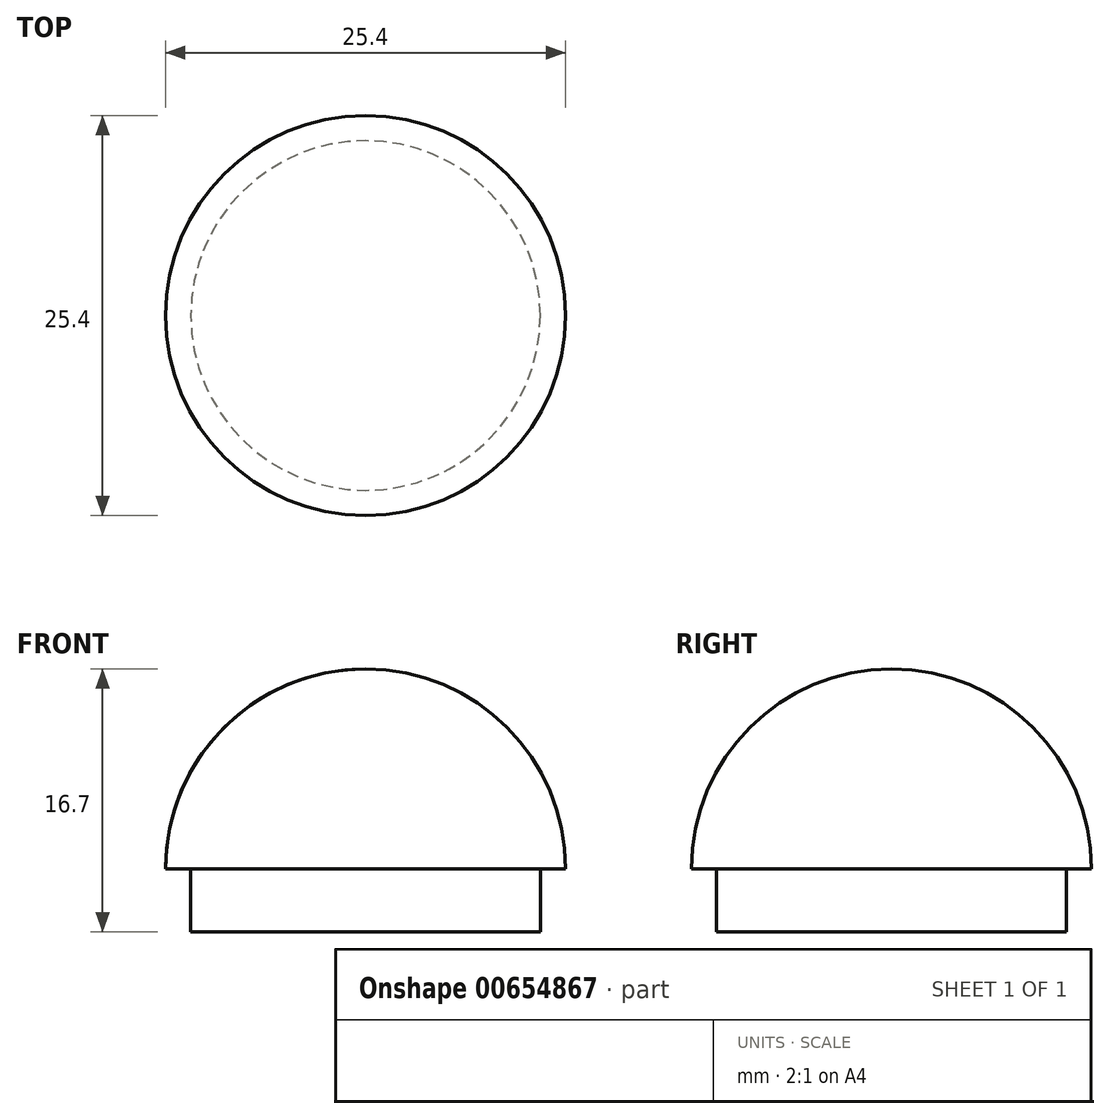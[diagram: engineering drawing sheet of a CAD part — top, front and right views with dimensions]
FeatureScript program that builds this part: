
annotation { "Feature Type Name" : "Feature", "Feature Type Description" : "" }
export const myFeature = defineFeature(function(context is Context, id is Id, definition is map)
    precondition{}
    {
        {
            var Q0;
            Q0=qCreatedBy(makeId("Front.planeOp"),FACE);
            var sketch = newSketch(context, id + "F0", { "sketchPlane" : qUnion([Q0])});
            skLineSegment(sketch, "E0", {"start": v(0, 0) * mm, "end": v(-11.1, 0) * mm});
            skLineSegment(sketch, "E1", {"start": v(-11.1, 0) * mm, "end": v(-11.1, 4) * mm});
            skLineSegment(sketch, "E2", {"start": v(-11.1, 4) * mm, "end": v(-12.7, 4) * mm});
            skLineSegment(sketch, "E3.MirrorCS", {"start": v(11.1, 4) * mm, "end": v(12.7, 4) * mm});
            skLineSegment(sketch, "E4.MirrorCS", {"start": v(11.1, 0) * mm, "end": v(11.1, 4) * mm});
            skLineSegment(sketch, "E5.MirrorCS", {"start": v(0, 0) * mm, "end": v(11.1, 0) * mm});
            skArc(sketch, "E6", {"start": v(12.7, 4) * mm, "mid": v(0, 16.7) * mm, "end": v(-12.7, 4) * mm});
            skLineSegment(sketch, "E7", {"start": v(0, 0) * mm, "end": v(0, 16.7) * mm});
            skSolve(sketch);
        }
        {
            var Q0;
            Q0=makeQuery(id+"F0.imprint","IMPRINT",FACE,{"disambiguationData":[TD([[makeQuery(id+"F0.imprint","IMPRINT",EDGE,{"derivedFrom":sQuery(id+"F0.wireOp",EDGE,"E0")}),-1.0]])]});
            var Q1;
            Q1=sQuery(id+"F0.wireOp",EDGE,"E7");
            revolve(context, id + "F1", {"entities" : qUnion([Q0]), "axis" : qUnion([Q1]), "revolveType" : RevolveType.FULL});
        }
    });
